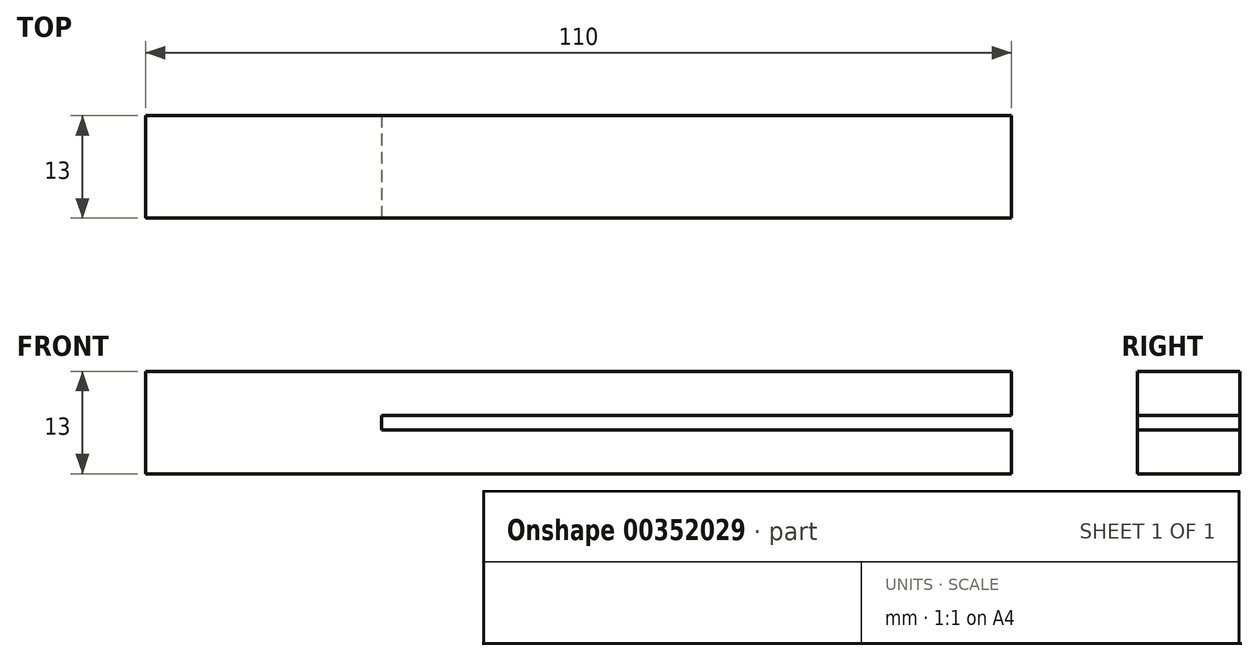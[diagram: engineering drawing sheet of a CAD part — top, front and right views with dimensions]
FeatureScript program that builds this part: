
annotation { "Feature Type Name" : "Feature", "Feature Type Description" : "" }
export const myFeature = defineFeature(function(context is Context, id is Id, definition is map)
    precondition{}
    {
        {
            var Q0;
            Q0=qCreatedBy(makeId("Right.planeOp"),FACE);
            var sketch = newSketch(context, id + "F0", { "sketchPlane" : qUnion([Q0])});
            skLineSegment(sketch, "E0.bottom", {"start": v(-6.5, 6.5) * mm, "end": v(6.5, 6.5) * mm});
            skLineSegment(sketch, "E0.top", {"start": v(-6.5, -6.5) * mm, "end": v(6.5, -6.5) * mm});
            skLineSegment(sketch, "E0.left", {"start": v(-6.5, 6.5) * mm, "end": v(-6.5, -6.5) * mm});
            skLineSegment(sketch, "E0.right", {"start": v(6.5, 6.5) * mm, "end": v(6.5, -6.5) * mm});
            skSolve(sketch);
        }
        {
            var Q0;
            Q0=qSketchRegion(id+"F0",true);
            extrude(context, id + "F1", {"entities" : qUnion([Q0]), "depth" : 110 * mm});
        }
        {
            var Q0;
            Q0=qCreatedBy(makeId("Right.planeOp"),FACE);
            cPlane(context, id + "F2", {"entities" : qUnion([Q0]), "cplaneType" : CPlaneType.OFFSET, "offset" : 110 * mm, "width" : 150 * mm, "height" : 150 * mm});
        }
        {
            var Q0;
            Q0=qCreatedBy(id+"F2.planeOp",FACE);
            var sketch = newSketch(context, id + "F3", { "sketchPlane" : qUnion([Q0])});
            skLineSegment(sketch, "E1", {"start": v(-6.5, 0.9) * mm, "end": v(-6.5, -0.9) * mm});
            skLineSegment(sketch, "E2", {"start": v(-6.5, -0.9) * mm, "end": v(6.5, -0.9) * mm});
            skLineSegment(sketch, "E3", {"start": v(6.5, -0.9) * mm, "end": v(6.5, 0.9) * mm});
            skLineSegment(sketch, "E4", {"start": v(6.5, 0.9) * mm, "end": v(-6.5, 0.9) * mm});
            skSolve(sketch);
        }
        {
            var Q0;
            Q0=qSketchRegion(id+"F3",true);
            extrude(context, id + "F4", {"entities" : qUnion([Q0]), "operationType" : NewBodyOperationType.REMOVE, "oppositeDirection" : true, "depth" : 80 * mm});
        }
    });
